# Revit family: IS_UltraflatEvo_T5432_BIM_NL
name_source: partatom
category: Plumbing Fixtures
units: mm (PartAtom-declared; Revit-internal decimal feet)

## family parameters
Cut with Voids When Loaded = No
Host = Face
Maintain Annotation Orientation = No
OmniClass Number = 23.45.05.14.17.14
OmniClass Title = Shower Receptors
Part Type = Normal
Room Calculation Point = No
Round Connector Dimension = Use Diameter
Shared = No

## types (2) — shared parameters
Accesoires = https://www.idealstandard.nl
Accessories = https://www.idealstandard.nl
Afmetingen = 1600 x 900 x 35 mm
AfstandsEenheid = Millimeter
AreaUnits = Millimeter
Assembly Code = C1030200
AssetType = Fixed
BIMObjectName = ISI_IdealStandard_Showers_UltraflatEvo_T5432
BREEAM = No
Beschrijvinggarantie = Herstellergarantie
Brand = Ideal Standard
CodePerformance = EN14527:2006 + A1:2010
CurrencyUnit = €
Default Elevation = 1219 mm
DrainSize = 90 mm  [stored 0.295276 ft]
DurationUnit = year
DuurEenheid = Jahr
ECA = No
EPD = https://www.idealstandard.nl
ExpectedLife = 20
Garantieunits = Jahr
GemaaktOp = 2023-12-08
HasRiserKit = No
HasTray = Yes
Hoogte = 35,0000662522567
Hulp = https://www.idealstandard.nl
IfcExportAs = IfcSanitaryTerminalType
IfcExportType = SHOWER
Installatieinstructies = https://www.idealstandard.nl
InstallationInstructions = https://www.idealstandard.nl
Lengte = 900 mm  [stored 2.95276 ft]
LinearUnits = millimeters
Manufacturer = Ideal Standard
ManufacturerURL = https://www.idealstandard.nl
Materiaal = Acrylbeschichtetes ABS und Polymerharz
Material = Acrylic capped ABS & polymer resin
Merk = Ideal Standard
NBSDescription = Shower trays
NBSReference = 45-35-70/336
Name = Showers_T5432_UltraflatEvo_IdealStandard
NettWeight = 56,20 KG
NominalDepth = 900 mm  [stored 2.95276 ft]
NominalHeight = 35 mm
NominalLength = 900 mm  [stored 2.95276 ft]
NominalWidth = 1600 mm  [stored 5.24934 ft]
ProductInformation = https://www.idealstandard.nl
Shape = Rectangular
ShowerType = Individual
Size = 1600 x 900 x 35 mm
Space = Internal
SpareParts = https://www.idealstandard.nl
TMV3 = No
Telefoonnummer = 077 355 08 08
Typeconnectie = Installation
URL = https://www.idealstandard.nl
Uniclass2015Code = Pr_40_20_06_84
Uniclass2015Description = Shower trays
Uniclass2015Reference = Pr_40_20_06_84
Uniclass2015Version = Products v1.1
ValutaEenheid = €
Versie = 1
Version = 1
VolumeUnits = Litres
Volumeunits = Liter
Vorm = Rechteckig
WRAS = No
WarrantyDescription = Manufacturers warranty
WarrantyDurationParts = 25
WarrantyDurationUnit = year
WarrantyGuarantorParts = https://www.idealstandard.nl
WasteMatl = <By Category>
WaterEfficientProduct = No
Wisselstukken = https://www.idealstandard.nl
zero-valued in all types: Breedte, BrutoGewicht, Diepte, MaterialThickness, Nettogewicht, Vervangingskosten

## per-type parameters (varying)
| type | Afwerking | Artikelnummer | Artikelomschrijving | BarCode | Barcode | Color | Description | Eigenschappen | Features | Finish | Kleur | Model | ModelNumber | ModelReference | TrayMatl |
| T5432FO - ULTRA FLAT EVO SHT 160X90 RECT SIL WH | Seidenweiß | T5432FO | ULTRA FLAT EVO Rechteckige Duschwanne 900 mm. seidenweiß. | 8014140510987 | 8014140510987 | Silk White | ULTRA FLAT EVO Rectangular shower tray 900 mm. silk white. | ULTRA FLAT EVO / Rechteckige Duschwanne 1600x900x35 mm in seidenweißer Ausführung, ohne Ablaufgarnitur / Antibakteriell, zugängliches Design, Schneidbarkeit, einfache Reparatur, 35/36 mm Höhe | ULTRA FLAT EVO / Rectangular shower tray 1600x900x35 mm in silk white finish, no waste / Antibacterial, Accessible design, Cutability, Easy repair, 35/36mm height | Silk White | Seidenweiß | T5432FO | T5432FO | ULTRA FLAT EVO Rectangular shower tray 900 mm. silk white. | Silk_White_FO |
| T5432FG - ULTRA FLAT EVO SHT 160X90 RECT S.GREY | Seidengrau | T5432FG | ULTRA FLAT EVO Rechteckige Duschwanne 900 mm. Seidengrau. | 8014140510970 | 8014140510970 | Silk Grey | ULTRA FLAT EVO Rectangular shower tray 900 mm. silk grey. | ULTRA FLAT EVO / Rechteckige Duschwanne 1600x900x35 mm in seidengrauer Ausführung, ohne Ablaufgarnitur / Antibakteriell, zugängliches Design, Schneidbarkeit, einfache Reparatur, 35/36 mm Höhe | ULTRA FLAT EVO / Rectangular shower tray 1600x900x35 mm in silk grey finish, no waste / Antibacterial, Accessible design, Cutability, Easy repair, 35/36mm height | Silk Grey | Seidengrau | T5432FG | T5432FG | ULTRA FLAT EVO Rectangular shower tray 900 mm. silk grey. | Silk_Grey_FG |

note: [stored X ft] marks values corroborated as IEEE doubles in the binary element streams (Revit-internal decimal feet)

## geometry (parser evidence)
native form markers: Sweep x2
no freeform markers — native parametric forms only
